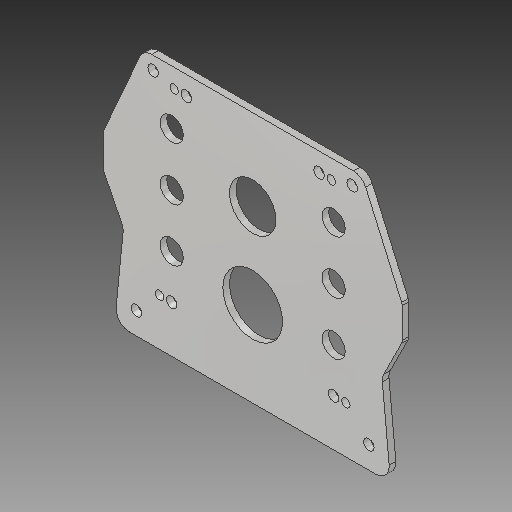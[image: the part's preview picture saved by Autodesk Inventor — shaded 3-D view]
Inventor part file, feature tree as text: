
AUTODESK INVENTOR PART (.ipt)
format: ipt  version: 2018 (Build 220112000, 112)  size: 3,773,952 bytes
history: native  units: in
note: dims shown in document units (in); Inventor stores cm internally (conversion verified against a paired STEP export)
features: other x11, hole x6, sketch x5, sheet_metal_op x3, chamfer x2, mirror x1
ambient origin geometry x8: Origin, YZ Plane, XZ Plane, XY Plane, X Axis, Y Axis, Z Axis, Center Point
bodies: Solid1 (feature_tree), Solid2 (feature_tree)
feature tree (28):
  other  "am-2230+TM+Flat+Shaft+Plate.ipt"
  other  "TM Housing.ipt"
  sheet_metal_op  "Face1"
  sketch  "Sketch3"  dims[d3=0.4375in d4=0.8745in]
  hole  "Hole1"  [1 undecoded]
  hole  "Hole2"  [1 undecoded]
  hole  "Hole3"  [1 undecoded]
  sketch  "Sketch4"  dims[d5=1.1245in d6=0.8745in]
  hole  "Hole4"  [1 undecoded]
  hole  "Hole5"  [1 undecoded]
  hole  "Hole6"  [1 undecoded]
  chamfer  "Corner Round1"
  sheet_metal_op  "Face2"
  mirror  "Mirror1"
  chamfer  "Corner Round2"
  other  "TaggingFeature1"
  sketch  "Sketch2"  dims[d1=0.3937in d2=0.125in]
  other  "Plate1"
  sketch  "Sketch5"  dims[d7=0.75in d8=0.375in d9=0.25in d10=0.5635in d11=0.125in d12=0.8108in]
  other  "Solid1::TM Housing.ipt"
  other  "TaggingFeature2"
  sketch  "Sketch6"  dims[d13=1.1245in d14=0.75in d15=0.375in d16=0.25in d17=0.5635in d18=0.125in d19=0.8108in d20=0.4375in d21=0.75in d22=0.375in d23=0.25in d24=0.5635in d25=0.125in d26=0.8108in d27=0.16in d28=0.2in d29=0.16in d30=0.75in d31=0.375in d32=0.25in d33=0.5635in d34=0.125in d35=0.8108in d36=0.2in d37=0.75in d38=0.375in d39=0.25in d40=0.5635in d41=0.125in d42=0.8108in d43=4.7372in d44=0.2in d45=0.75in d46=0.375in d47=0.25in d48=0.5635in d49=0.125in d50=0.8108in d51=0.25in d52=0.3937in d53=0.0625in d54=0.0625in d55=0.03in d56=0.125in d57=0.125in d58=0.0625in d59=0.25in d60=0.125in d61=0.25in]
  other  "Plate2"
  sheet_metal_op  "Bend1"
  other  "Solid1::am-2230+TM+Flat+Shaft+Plate.ipt"
  other  "Srf2"
  other  "am-2230+TM+Flat+Shaft+Plate.ipt_Bodies"
  other  "TM Housing.ipt_Bodies"
note: 6 required parameter values undecoded (feature->parameter linkage not recoverable at this tier; creation-order binding heuristic only, values carry confidence <= 0.55)
